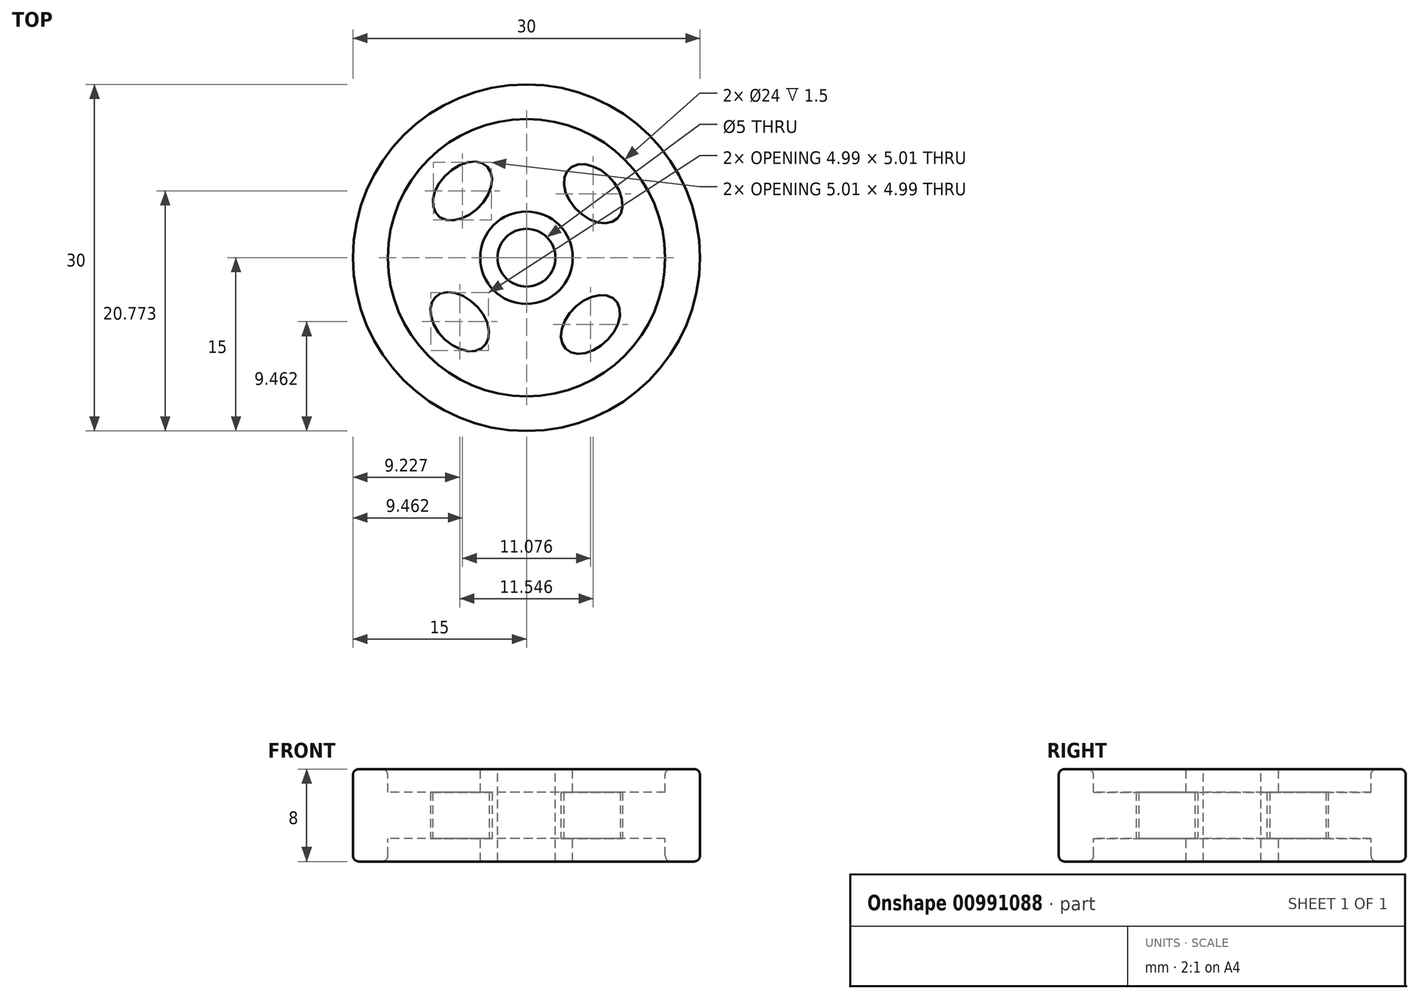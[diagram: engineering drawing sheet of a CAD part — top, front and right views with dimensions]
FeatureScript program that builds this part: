
annotation { "Feature Type Name" : "Feature", "Feature Type Description" : "" }
export const myFeature = defineFeature(function(context is Context, id is Id, definition is map)
    precondition{}
    {
        {
            var Q0;
            Q0=qCreatedBy(makeId("Front.planeOp"),FACE);
            var sketch = newSketch(context, id + "F0", { "sketchPlane" : qUnion([Q0])});
            skLineSegment(sketch, "E0", {"start": v(0, 0) * mm, "end": v(4, 0) * mm});
            skLineSegment(sketch, "E1", {"start": v(4, 0) * mm, "end": v(4, 2) * mm});
            skLineSegment(sketch, "E2", {"start": v(4, 2) * mm, "end": v(12, 2) * mm});
            skLineSegment(sketch, "E3", {"start": v(12, 2) * mm, "end": v(12, 0) * mm});
            skLineSegment(sketch, "E4", {"start": v(12, 0) * mm, "end": v(15, 0) * mm});
            skLineSegment(sketch, "E5", {"start": v(15, 0) * mm, "end": v(15, 8) * mm});
            skLineSegment(sketch, "E6", {"start": v(15, 8) * mm, "end": v(12, 8) * mm});
            skLineSegment(sketch, "E7", {"start": v(12, 8) * mm, "end": v(12, 6) * mm});
            skLineSegment(sketch, "E8", {"start": v(12, 6) * mm, "end": v(4, 6) * mm});
            skLineSegment(sketch, "E9", {"start": v(4, 6) * mm, "end": v(4, 8) * mm});
            skLineSegment(sketch, "E10", {"start": v(4, 8) * mm, "end": v(0, 8) * mm});
            skLineSegment(sketch, "E11", {"start": v(0, 8) * mm, "end": v(0, 0) * mm});
            skSolve(sketch);
        }
        {
            var Q0;
            Q0 = qSketchRegion(id + "F0", true);
            var Q1;
            Q1=sQuery(id+"F0.wireOp",EDGE,"E11");
            revolve(context, id + "F1", {"surfaceOperationType" : NewSurfaceOperationType.NEW, "entities" : qUnion([Q0]), "axis" : qUnion([Q1]), "revolveType" : RevolveType.FULL});
        }
        {
            var Q0;
            Q0=makeQuery(id+"F1.opRevolve","SWEPT_FACE",FACE,{"disambiguationData":[OSD([sQuery(id+"F0.wireOp",EDGE,"E8")])]});
            var sketch = newSketch(context, id + "F2", { "sketchPlane" : qUnion([Q0])});
            skEllipse(sketch, "E12", {"center": v(5.77, 5.54) * mm, "majorRadius": 3 * mm, "minorRadius": 2 * mm, "majorAxis": v(0.7, -0.71)});
            skLineSegment(sketch, "E13", {"start": v(0, 0) * mm, "end": v(5.77, 5.54) * mm});
            skEllipse(sketch, "E14.1.0", {"center": v(-5.54, 5.77) * mm, "majorRadius": 3 * mm, "minorRadius": 2 * mm, "majorAxis": v(0.71, 0.7)});
            skEllipse(sketch, "E14.2.0", {"center": v(-5.77, -5.54) * mm, "majorRadius": 3 * mm, "minorRadius": 2 * mm, "majorAxis": v(-0.7, 0.71)});
            skEllipse(sketch, "E14.3.0", {"center": v(5.54, -5.77) * mm, "majorRadius": 3 * mm, "minorRadius": 2 * mm, "majorAxis": v(-0.71, -0.7)});
            skPoint(sketch, "E14.center", {"position": v(0, 0) * mm});
            skSolve(sketch);
        }
        {
            var Q0;
            Q0=makeQuery(id+"F2.imprint","IMPRINT",FACE,{"disambiguationData":[TD([[makeQuery(id+"F2.imprint","IMPRINT",EDGE,{"derivedFrom":sQuery(id+"F2.wireOp",EDGE,"E14.1.0")}),1.0]])]});
            var Q1;
            Q1=makeQuery(id+"F2.imprint","IMPRINT",FACE,{"disambiguationData":[TD([[makeQuery(id+"F2.imprint","IMPRINT",EDGE,{"derivedFrom":sQuery(id+"F2.wireOp",EDGE,"E14.2.0")}),1.0]])]});
            var Q2;
            Q2=makeQuery(id+"F2.imprint","IMPRINT",FACE,{"disambiguationData":[TD([[makeQuery(id+"F2.imprint","IMPRINT",EDGE,{"derivedFrom":sQuery(id+"F2.wireOp",EDGE,"E14.3.0")}),1.0]])]});
            var Q3;
            Q3=makeQuery(id+"F2.imprint","IMPRINT",FACE,{"disambiguationData":[TD([[makeQuery(id+"F2.imprint","IMPRINT",EDGE,{"derivedFrom":sQuery(id+"F2.wireOp",EDGE,"E12")}),1.0]])]});
            var Q4;
            Q4=sQuery(id+"F2.wireOp",EDGE,"E14.1.0");
            var Q5;
            Q5=sQuery(id+"F2.wireOp",EDGE,"E14.2.0");
            var Q6;
            Q6=sQuery(id+"F2.wireOp",EDGE,"E14.3.0");
            var Q7;
            Q7=sQuery(id+"F2.wireOp",EDGE,"E12");
            extrude(context, id + "F3", {"entities" : qUnion([Q0, Q1, Q2, Q3]), "operationType" : NewBodyOperationType.REMOVE, "surfaceEntities" : qUnion([Q4, Q5, Q6, Q7]), "endBound" : BoundingType.THROUGH_ALL, "oppositeDirection" : true, "depth" : 25 * mm, "offsetDistance" : 25 * mm});
        }
        {
            var Q0;
            Q0=makeQuery(id+"F1.opRevolve","SWEPT_FACE",FACE,{"disambiguationData":[OSD([sQuery(id+"F0.wireOp",EDGE,"E10")])]});
            var sketch = newSketch(context, id + "F4", { "sketchPlane" : qUnion([Q0])});
            skPoint(sketch, "E15", {"position": v(0, 0) * mm});
            skSolve(sketch);
        }
        {
            var Q0;
            Q0=sQuery(id+"F4.wireOp",VERTEX,"E15");
            var Q1;
            Q1=makeQuery(id+"F1.opRevolve","SWEPT_BODY",BODY,{"disambiguationData":[OSD([sQuery(id+"F0.wireOp",EDGE,"E0"),sQuery(id+"F0.wireOp",EDGE,"E1"),sQuery(id+"F0.wireOp",EDGE,"E2"),sQuery(id+"F0.wireOp",EDGE,"E3"),sQuery(id+"F0.wireOp",EDGE,"E4"),sQuery(id+"F0.wireOp",EDGE,"E5"),sQuery(id+"F0.wireOp",EDGE,"E6"),sQuery(id+"F0.wireOp",EDGE,"E7"),sQuery(id+"F0.wireOp",EDGE,"E8"),sQuery(id+"F0.wireOp",EDGE,"E9"),sQuery(id+"F0.wireOp",EDGE,"E10"),sQuery(id+"F0.wireOp",EDGE,"E11")])]});
            hole(context, id + "F5", {"style" : HoleStyle.SIMPLE, "endStyle" : HoleEndStyle.THROUGH, "holeDiameter" : 5 * mm, "majorDiameter" : 5 * mm, "isTappedThrough" : true, "tappedDepth" : 12 * mm, "tapClearance" : 3, "locations" : qUnion([Q0]), "scope" : qUnion([Q1])});
        }
        {
            var Q0;
            Q0=makeQuery(id+"F1.opRevolve","SWEPT_EDGE",EDGE,{"disambiguationData":[OSD([sQuery(id+"F0.wireOp",EDGE,"E5"),sQuery(id+"F0.wireOp",EDGE,"E6")])]});
            var Q1;
            Q1=makeQuery(id+"F1.opRevolve","SWEPT_EDGE",EDGE,{"disambiguationData":[OSD([sQuery(id+"F0.wireOp",EDGE,"E4"),sQuery(id+"F0.wireOp",EDGE,"E5")])]});
            var Q2;
            Q2=makeQuery(id+"F1.opRevolve","SWEPT_EDGE",EDGE,{"disambiguationData":[OSD([sQuery(id+"F0.wireOp",EDGE,"E6"),sQuery(id+"F0.wireOp",EDGE,"E7")])]});
            var Q3;
            Q3=makeQuery(id+"F1.opRevolve","SWEPT_EDGE",EDGE,{"disambiguationData":[OSD([sQuery(id+"F0.wireOp",EDGE,"E3"),sQuery(id+"F0.wireOp",EDGE,"E4")])]});
            fillet(context, id + "F6", {"entities" : qUnion([Q0, Q1, Q2, Q3]), "radius" : 0.5 * mm, "tangentPropagation" : true, "allowEdgeOverflow" : false});
        }
    });
